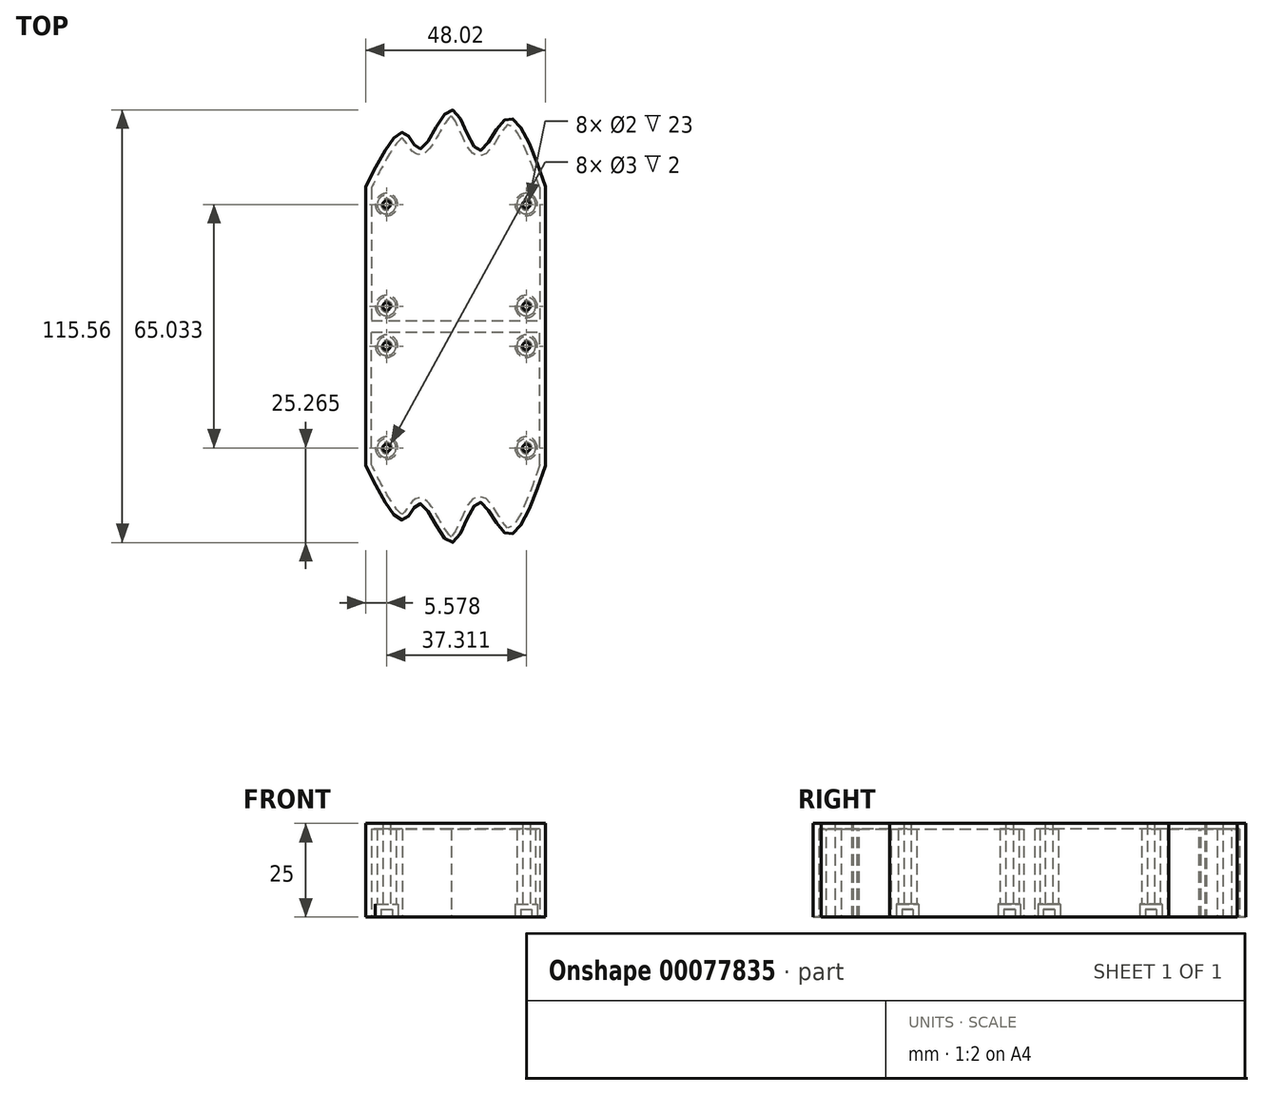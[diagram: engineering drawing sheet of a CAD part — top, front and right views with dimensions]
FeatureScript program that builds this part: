
annotation { "Feature Type Name" : "Feature", "Feature Type Description" : "" }
export const myFeature = defineFeature(function(context is Context, id is Id, definition is map)
    precondition{}
    {
        {
            var Q0;
            Q0=qCreatedBy(makeId("Top.planeOp"),FACE);
            var sketch = newSketch(context, id + "F0", { "sketchPlane" : qUnion([Q0])});
            skLineSegment(sketch, "E0.bottom", {"start": v(-63.57, 42.05) * mm, "end": v(-15.55, 42.05) * mm});
            skLineSegment(sketch, "E0.top", {"start": v(-63.57, 4.77) * mm, "end": v(-15.55, 4.77) * mm});
            skLineSegment(sketch, "E0.left", {"start": v(-63.57, 42.05) * mm, "end": v(-63.57, 4.77) * mm});
            skLineSegment(sketch, "E0.right", {"start": v(-15.55, 42.05) * mm, "end": v(-15.55, 4.77) * mm});
            skPoint(sketch, "E1", {"position": v(-58, 37.29) * mm});
            skPoint(sketch, "E2", {"position": v(-58, 10.07) * mm});
            skPoint(sketch, "E3", {"position": v(-20.68, 10.07) * mm});
            skPoint(sketch, "E4", {"position": v(-20.68, 37.29) * mm});
            skFitSpline(sketch, "E5", {"points": [v(-15.55, 42.05) * mm, v(-26.1, 60.17) * mm, v(-33.46, 51.73) * mm, v(-40.6, 62.55) * mm, v(-48.95, 52.15) * mm, v(-53.1, 56.37) * mm, v(-63.57, 42.05) * mm], "startDerivative": vector(-50.4, 142.6) * mm, "endDerivative": vector(-60.85, -121.6) * mm});
            skSolve(sketch);
        }
        {
            var Q0;
            Q0=makeQuery(id+"F0.imprint","IMPRINT",FACE,{"disambiguationData":[TD([[makeQuery(id+"F0.imprint","IMPRINT",EDGE,{"derivedFrom":sQuery(id+"F0.wireOp",EDGE,"E0.bottom")}),-1.0]])]});
            var Q1;
            Q1=makeQuery(id+"F0.imprint","IMPRINT",FACE,{"disambiguationData":[TD([[makeQuery(id+"F0.imprint","IMPRINT",EDGE,{"derivedFrom":sQuery(id+"F0.wireOp",EDGE,"E0.bottom")}),1.0]])]});
            extrude(context, id + "F1", {"entities" : qUnion([Q0, Q1]), "depth" : 25 * mm});
        }
        {
            var Q0;
            Q0=sQuery(id+"F0.wireOp",VERTEX,"E1");
            var Q1;
            Q1=sQuery(id+"F0.wireOp",VERTEX,"E2");
            var Q2;
            Q2=sQuery(id+"F0.wireOp",VERTEX,"E3");
            var Q3;
            Q3=sQuery(id+"F0.wireOp",VERTEX,"E4");
            var Q4;
            Q4=makeQuery(id+"F1.opExtrude","SWEPT_BODY",BODY,{"disambiguationData":[OSD([sQuery(id+"F0.wireOp",EDGE,"E0.bottom"),sQuery(id+"F0.wireOp",EDGE,"E0.top"),sQuery(id+"F0.wireOp",EDGE,"E0.left"),sQuery(id+"F0.wireOp",EDGE,"E0.right")])]});
            hole(context, id + "F2", {"style" : HoleStyle.C_BORE, "endStyle" : HoleEndStyle.THROUGH, "oppositeDirection" : true, "holeDiameter" : 2 * mm, "cBoreDiameter" : 3 * mm, "cBoreDepth" : 2 * mm, "startFromSketch" : true, "locations" : qUnion([Q0, Q1, Q2, Q3]), "scope" : qUnion([Q4]), "isTappedThrough" : true});
        }
        {
            var Q0;
            Q0=makeQuery(id+"F1.opExtrude","CAP_FACE",FACE,{"disambiguationData":[OSD([sQuery(id+"F0.wireOp",EDGE,"E0.bottom"),sQuery(id+"F0.wireOp",EDGE,"E0.top"),sQuery(id+"F0.wireOp",EDGE,"E0.left"),sQuery(id+"F0.wireOp",EDGE,"E0.right")])],"isStart":true});
            shell(context, id + "F3", {"entities" : qUnion([Q0]), "thickness" : 1.5 * mm});
        }
        {
            var Q0;
            Q0=makeQuery(id+"F1.opExtrude","SWEPT_BODY",BODY,{"disambiguationData":[OSD([sQuery(id+"F0.wireOp",EDGE,"E0.bottom"),sQuery(id+"F0.wireOp",EDGE,"E0.top"),sQuery(id+"F0.wireOp",EDGE,"E0.left"),sQuery(id+"F0.wireOp",EDGE,"E0.right")])]});
            var Q1;
            Q1=makeQuery(id+"F1.opExtrude","SWEPT_FACE",FACE,{"disambiguationData":[OSD([sQuery(id+"F0.wireOp",EDGE,"E0.top")])]});
            mirror(context, id + "F4", {"operationType" : NewBodyOperationType.ADD, "entities" : qUnion([Q0]), "mirrorPlane" : qUnion([Q1])});
        }
    });
